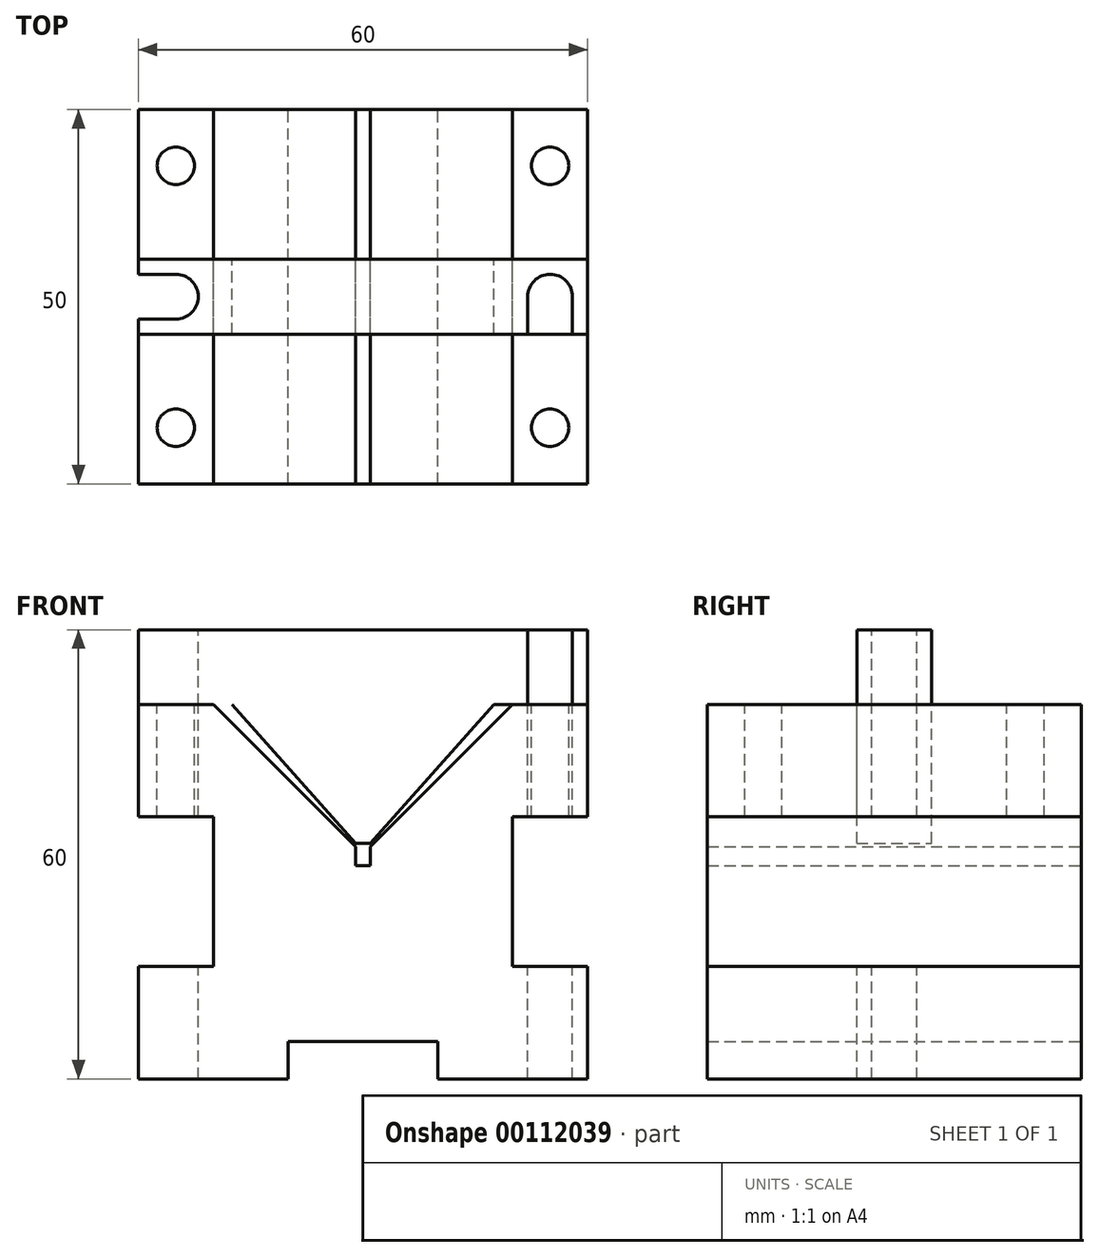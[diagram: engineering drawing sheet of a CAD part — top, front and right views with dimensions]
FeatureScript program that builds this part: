
annotation { "Feature Type Name" : "Feature", "Feature Type Description" : "" }
export const myFeature = defineFeature(function(context is Context, id is Id, definition is map)
    precondition{}
    {
        {
            var Q0;
            Q0=qCreatedBy(makeId("Front.planeOp"),FACE);
            var sketch = newSketch(context, id + "F0", { "sketchPlane" : qUnion([Q0])});
            skLineSegment(sketch, "E0.bottom", {"start": v(30, 25) * mm, "end": v(-30, 25) * mm});
            skLineSegment(sketch, "E0.top", {"start": v(30, -25) * mm, "end": v(-30, -25) * mm});
            skLineSegment(sketch, "E0.left", {"start": v(30, 25) * mm, "end": v(30, -25) * mm});
            skLineSegment(sketch, "E0.right", {"start": v(-30, 25) * mm, "end": v(-30, -25) * mm});
            skPoint(sketch, "E0.middle", {"position": v(0, 0) * mm});
            skLineSegment(sketch, "E1.bottom", {"start": v(-20, 10) * mm, "end": v(-40, 10) * mm});
            skLineSegment(sketch, "E1.top", {"start": v(-20, -10) * mm, "end": v(-40, -10) * mm});
            skLineSegment(sketch, "E1.left", {"start": v(-20, 10) * mm, "end": v(-20, -10) * mm});
            skLineSegment(sketch, "E1.right", {"start": v(-40, 10) * mm, "end": v(-40, -10) * mm});
            skPoint(sketch, "E1.middle", {"position": v(-30, 0) * mm});
            skLineSegment(sketch, "E2", {"start": v(0, 25) * mm, "end": v(0, -25) * mm, "construction": true});
            skLineSegment(sketch, "E3.MirrorCS", {"start": v(20, -10) * mm, "end": v(40, -10) * mm});
            skLineSegment(sketch, "E4.MirrorCS", {"start": v(20, 10) * mm, "end": v(40, 10) * mm});
            skLineSegment(sketch, "E5.MirrorCS", {"start": v(20, 10) * mm, "end": v(20, -10) * mm});
            skPoint(sketch, "E6.middle", {"position": v(0, -25) * mm});
            skLineSegment(sketch, "E7", {"start": v(-20, 25) * mm, "end": v(0, 5) * mm});
            skLineSegment(sketch, "E8.MirrorCS", {"start": v(20, 25) * mm, "end": v(0, 5) * mm});
            skLineSegment(sketch, "E9.bottom", {"start": v(1, 3.5) * mm, "end": v(-1, 3.5) * mm});
            skLineSegment(sketch, "E9.top", {"start": v(1, 6.5) * mm, "end": v(-1, 6.5) * mm});
            skLineSegment(sketch, "E9.left", {"start": v(1, 3.5) * mm, "end": v(1, 6.5) * mm});
            skLineSegment(sketch, "E9.right", {"start": v(-1, 3.5) * mm, "end": v(-1, 6.5) * mm});
            skPoint(sketch, "E9.middle", {"position": v(0, 5) * mm});
            skLineSegment(sketch, "E10.bottom", {"start": v(10, -20) * mm, "end": v(-10, -20) * mm});
            skLineSegment(sketch, "E10.top", {"start": v(10, -30) * mm, "end": v(-10, -30) * mm});
            skLineSegment(sketch, "E10.left", {"start": v(10, -20) * mm, "end": v(10, -30) * mm});
            skLineSegment(sketch, "E10.right", {"start": v(-10, -20) * mm, "end": v(-10, -30) * mm});
            skLineSegment(sketch, "E11", {"start": v(-30, 25) * mm, "end": v(-30, 35) * mm});
            skLineSegment(sketch, "E12", {"start": v(-30, 35) * mm, "end": v(30, 35) * mm});
            skLineSegment(sketch, "E13", {"start": v(30, 35) * mm, "end": v(30, 25) * mm});
            skLineSegment(sketch, "E14", {"start": v(-1, 6.5) * mm, "end": v(-17.5, 25) * mm});
            skLineSegment(sketch, "E15.MirrorCS", {"start": v(1, 6.5) * mm, "end": v(17.5, 25) * mm});
            skSolve(sketch);
        }
        {
            var Q0;
            {var subQ0=sQuery(id+"F0.wireOp",EDGE,"E1.left");Q0=makeQuery(id+"F0.imprint","IMPRINT",FACE,{"disambiguationData":[TD([[makeQuery(id+"F0.imprint","IMPRINT",EDGE,{"derivedFrom":subQ0}),1.0]])]});}
            extrude(context, id + "F1", {"entities" : qUnion([Q0]), "endBound" : BoundingType.SYMMETRIC, "depth" : 50 * mm});
        }
        {
            var Q0;
            {var subQ0=sQuery(id+"F0.wireOp",EDGE,"E0.bottom");Q0=makeQuery(id+"F1.opExtrude","SWEPT_FACE",FACE,{"disambiguationData":[OSD([subQ0]),TDD([makeQuery(id+"F0.imprint","IMPRINT",EDGE,{"disambiguationData":[TD([[makeQuery(id+"F0.imprint","INTERSECT",VERTEX,{"derivedFrom":[subQ0,sQuery(id+"F0.wireOp",EDGE,"E0.right")]}),1.0]])],"derivedFrom":subQ0})])]});}
            var sketch = newSketch(context, id + "F2", { "sketchPlane" : qUnion([Q0])});
            skPoint(sketch, "E16", {"position": v(-25, 0) * mm});
            skPoint(sketch, "E17", {"position": v(-25, -17.5) * mm});
            skPoint(sketch, "E18", {"position": v(-25, 17.5) * mm});
            skPoint(sketch, "E19.MirrorP", {"position": v(25, -17.5) * mm});
            skPoint(sketch, "E20.MirrorP", {"position": v(25, 0) * mm});
            skPoint(sketch, "E21.MirrorP", {"position": v(25, 17.5) * mm});
            skSolve(sketch);
        }
        {
            var Q0;
            Q0=sQuery(id+"F2.wireOp",VERTEX,"E17");
            var Q1;
            Q1=sQuery(id+"F2.wireOp",VERTEX,"E16");
            var Q2;
            Q2=sQuery(id+"F2.wireOp",VERTEX,"E18");
            var Q3;
            Q3=sQuery(id+"F2.wireOp",VERTEX,"E19.MirrorP");
            var Q4;
            Q4=sQuery(id+"F2.wireOp",VERTEX,"E20.MirrorP");
            var Q5;
            Q5=sQuery(id+"F2.wireOp",VERTEX,"E21.MirrorP");
            var Q6;
            Q6=makeQuery(id+"F1.opExtrude","SWEPT_BODY",BODY,{"disambiguationData":[OSD([sQuery(id+"F0.wireOp",EDGE,"E0.bottom"),sQuery(id+"F0.wireOp",EDGE,"E0.top"),sQuery(id+"F0.wireOp",EDGE,"E0.left"),sQuery(id+"F0.wireOp",EDGE,"E0.right"),sQuery(id+"F0.wireOp",EDGE,"E1.bottom"),sQuery(id+"F0.wireOp",EDGE,"E1.top"),sQuery(id+"F0.wireOp",EDGE,"E1.left"),sQuery(id+"F0.wireOp",EDGE,"E3.MirrorCS"),sQuery(id+"F0.wireOp",EDGE,"E4.MirrorCS"),sQuery(id+"F0.wireOp",EDGE,"E5.MirrorCS"),sQuery(id+"F0.wireOp",EDGE,"E6.bottom"),sQuery(id+"F0.wireOp",EDGE,"E6.left"),sQuery(id+"F0.wireOp",EDGE,"E6.right"),sQuery(id+"F0.wireOp",EDGE,"E7"),sQuery(id+"F0.wireOp",EDGE,"E8.MirrorCS"),sQuery(id+"F0.wireOp",EDGE,"E9.bottom"),sQuery(id+"F0.wireOp",EDGE,"E9.left"),sQuery(id+"F0.wireOp",EDGE,"E9.right")])]});
            hole(context, id + "F3", {"style" : HoleStyle.SIMPLE, "endStyle" : HoleEndStyle.BLIND, "standardTappedOrClearance" : lookupTablePath({ "standard" : "ISO", "engagement" : "75%", "pitch" : "1 mm", "size" : "M6", "type" : "Tapped" }), "standardBlindInLast" : lookupTablePath({ "standard" : "ISO", "engagement" : "75%", "pitch" : "1 mm", "size" : "M6", "type" : "Tapped" }), "holeDiameter" : 5 * mm, "holeDepth" : 15 * mm, "startFromSketch" : true, "locations" : qUnion([Q0, Q1, Q2, Q3, Q4, Q5]), "scope" : qUnion([Q6]), "majorDiameter" : 6 * mm});
        }
        {
            var Q0;
            Q0=makeQuery(id+"F0.imprint","IMPRINT",FACE,{"disambiguationData":[TD([[makeQuery(id+"F0.imprint","IMPRINT",EDGE,{"derivedFrom":sQuery(id+"F0.wireOp",EDGE,"E9.top")}),-1.0]])]});
            var Q1;
            {var subQ6=sQuery(id+"F0.wireOp",EDGE,"E11");Q1=makeQuery(id+"F0.imprint","IMPRINT",FACE,{"disambiguationData":[TD([[makeQuery(id+"F0.imprint","IMPRINT",EDGE,{"derivedFrom":subQ6}),-1.0]])]});}
            extrude(context, id + "F4", {"entities" : qUnion([Q0, Q1]), "endBound" : BoundingType.SYMMETRIC, "depth" : 10 * mm});
        }
        {
            var Q0;
            Q0=makeQuery(id+"F4.opExtrude","SWEPT_FACE",FACE,{"disambiguationData":[OSD([sQuery(id+"F0.wireOp",EDGE,"E12")])]});
            var sketch = newSketch(context, id + "F5", { "sketchPlane" : qUnion([Q0])});
            skCircle(sketch, "E22", {"center": v(-25, 0) * mm, "radius": 3 * mm});
            skPoint(sketch, "E22.centerSnap0", {"position": v(-30, 0) * mm});
            skCircle(sketch, "E23", {"center": v(25, 0) * mm, "radius": 3 * mm});
            skPoint(sketch, "E23.centerSnap0", {"position": v(30, 0) * mm});
            skLineSegment(sketch, "E24", {"start": v(-25, 3) * mm, "end": v(-30, 3) * mm});
            skLineSegment(sketch, "E25", {"start": v(-25, -3) * mm, "end": v(-30, -3) * mm});
            skLineSegment(sketch, "E26", {"start": v(22, 0) * mm, "end": v(22, -5) * mm});
            skLineSegment(sketch, "E27", {"start": v(28, 0) * mm, "end": v(28, -5) * mm});
            skSolve(sketch);
        }
        {
            var Q0;
            {var subQ0=sQuery(id+"F5.wireOp",EDGE,"E22");var subQ1=makeQuery(id+"F5.imprint","INTERSECT",VERTEX,{"derivedFrom":[subQ0,sQuery(id+"F5.wireOp",EDGE,"E24")]});Q0=makeQuery(id+"F5.imprint","IMPRINT",FACE,{"disambiguationData":[TD([[makeQuery(id+"F5.imprint","IMPRINT",EDGE,{"disambiguationData":[TD([[subQ1,-1.0]])],"derivedFrom":subQ0}),1.0]])]});}
            var Q1;
            {var subQ0=sQuery(id+"F5.wireOp",EDGE,"E24");Q1=makeQuery(id+"F5.imprint","IMPRINT",FACE,{"disambiguationData":[TD([[makeQuery(id+"F5.imprint","IMPRINT",EDGE,{"derivedFrom":subQ0}),1.0]])]});}
            var Q2;
            {var subQ0=sQuery(id+"F5.wireOp",EDGE,"E23");var subQ1=makeQuery(id+"F5.imprint","INTERSECT",VERTEX,{"derivedFrom":[subQ0,sQuery(id+"F5.wireOp",EDGE,"E26")]});Q2=makeQuery(id+"F5.imprint","IMPRINT",FACE,{"disambiguationData":[TD([[makeQuery(id+"F5.imprint","IMPRINT",EDGE,{"disambiguationData":[TD([[subQ1,1.0]])],"derivedFrom":subQ0}),1.0]])]});}
            var Q3;
            {var subQ0=sQuery(id+"F5.wireOp",EDGE,"E26");Q3=makeQuery(id+"F5.imprint","IMPRINT",FACE,{"disambiguationData":[TD([[makeQuery(id+"F5.imprint","IMPRINT",EDGE,{"derivedFrom":subQ0}),1.0]])]});}
            extrude(context, id + "F6", {"entities" : qUnion([Q0, Q1, Q2, Q3]), "operationType" : NewBodyOperationType.REMOVE, "endBound" : BoundingType.THROUGH_ALL, "oppositeDirection" : true, "depth" : 25 * mm});
        }
    });
